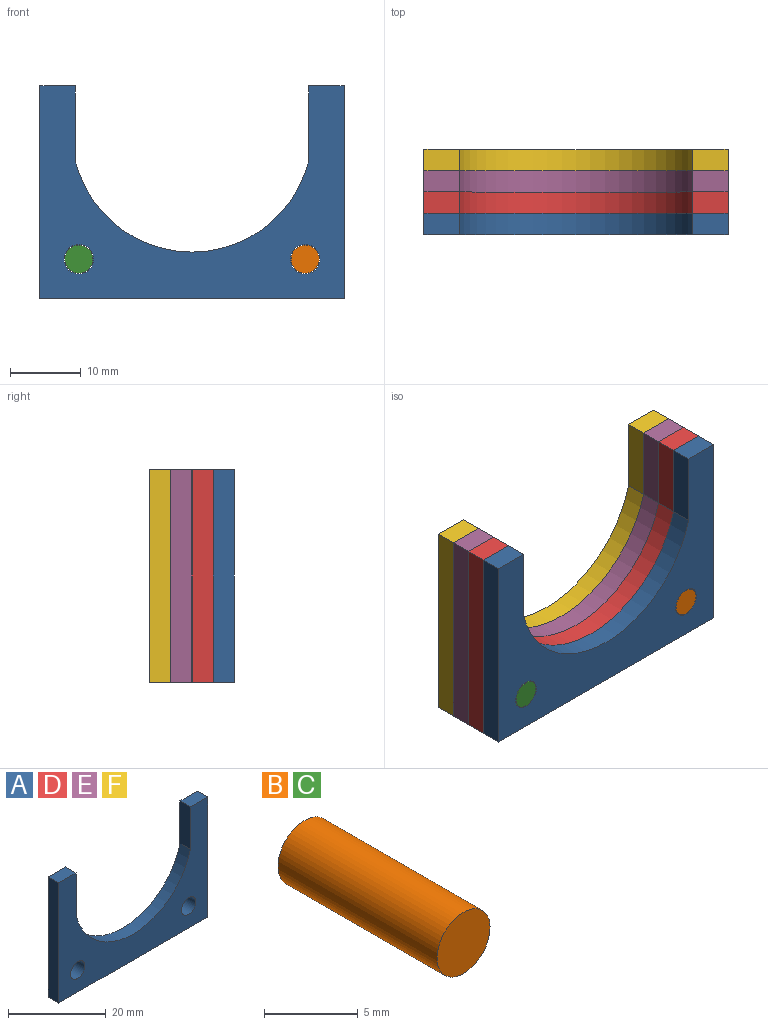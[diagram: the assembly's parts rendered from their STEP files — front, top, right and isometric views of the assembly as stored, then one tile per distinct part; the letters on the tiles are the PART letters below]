
ASSEMBLY  parts=6 mates=5
PART A: 12 faces, bbox 43x3x30 mm
  f0: plane 30x3mm, normal (-1,0,0), area 90mm2, adj f1,f9,f10,f11
  f1: plane 43x3mm, normal (0,0,-1), area 129mm2, adj f0,f2,f10,f11
  f2: plane 30x3mm, normal (1,0,0), area 90mm2, adj f1,f3,f10,f11
  f3: plane 5x3mm, normal (0,0,1), area 15mm2, adj f2,f4,f10,f11
  f4: plane 10.59x3mm, normal (-1,0,0), area 31.8mm2, adj f3,f5,f10,f11
  f5: cylinder r=17mm len=33mm, axis (0,1,0), area 135.4mm2, adj f4,f6,f10,f11
  f6: plane 10.59x3mm, normal (1,0,0), area 31.8mm2, adj f5,f9,f10,f11
  f7: cylinder r=2.08mm len=4.15mm, axis (0,1,0), area 39.1mm2, adj f10,f11
  f8: cylinder r=2.08mm len=4.15mm, axis (0,1,0), area 39.1mm2, adj f10,f11
  f9: plane 5x3mm, normal (0,0,1), area 15mm2, adj f0,f6,f10,f11
  f10: plane 43x30mm, normal (0,-1,0), area 597.2mm2, adj f0,f1,f2,f3,f4,f5,f6,f7
  f11: plane 43x30mm, normal (0,1,0), area 597.2mm2, adj f0,f1,f2,f3,f4,f5,f6,f7
PART B: 3 faces, bbox 4x12x4 mm
  f0: cylinder r=2mm len=12mm, axis (0,1,0), area 150.8mm2, adj f1,f2
  f1: plane 4x4mm, normal (0,-1,0), area 12.6mm2, adj f0
  f2: plane 4x4mm, normal (0,1,0), area 12.6mm2, adj f0
PART C: same geometry as B
PART D: same geometry as A
PART E: same geometry as A
PART F: same geometry as A
PLACE A t=(-22.45,-5.38,8.52)mm fixed
PLACE B t=(-6.45,3.62,-0.98)mm
PLACE C t=(-38.45,3.62,-0.98)mm
PLACE D t=(-22.45,-2.38,8.52)mm
PLACE E t=(-22.45,0.62,8.52)mm
PLACE F t=(-22.45,3.62,8.52)mm
MATE fastened D.f10 <-> A.f11  axis (0,-1,0) through (-0.95,-5.38,-6.48)mm
MATE fastened A.f8 <-> B.f0  axis (0,1,0) through (-6.45,-8.38,-0.98)mm
MATE fastened E.f11 <-> F.f10  axis (0,1,0) through (-0.95,0.62,-6.48)mm
MATE fastened A.f7 <-> C.f0  axis (0,1,0) through (-38.45,-8.38,-0.98)mm
MATE fastened D.f11 <-> E.f10  axis (0,1,0) through (-0.95,-2.38,-6.48)mm
